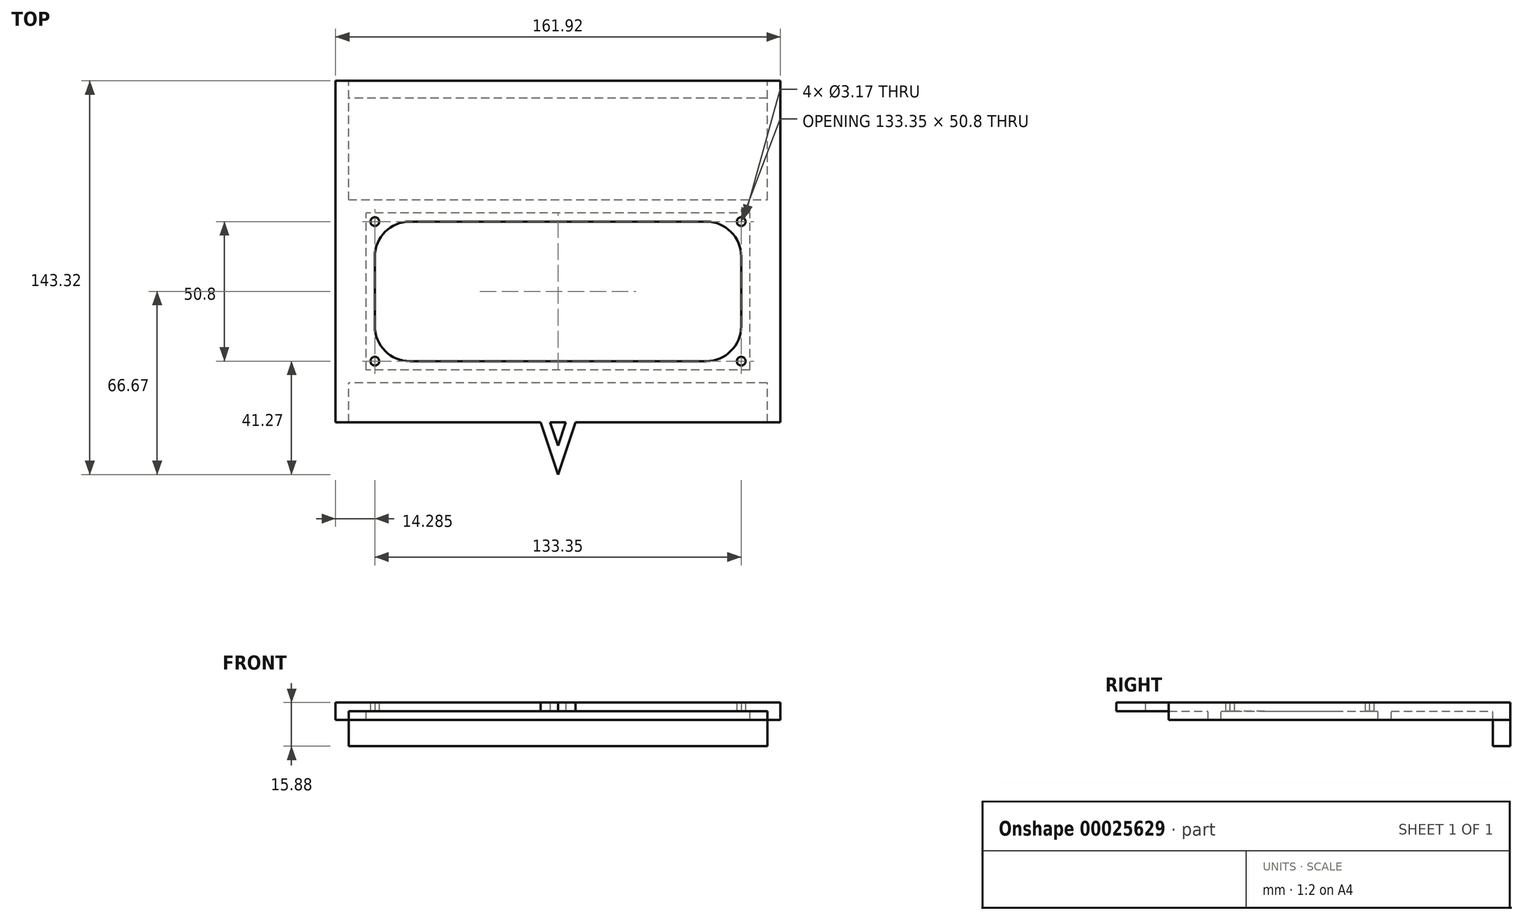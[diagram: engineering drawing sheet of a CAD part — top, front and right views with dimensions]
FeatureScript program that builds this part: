
annotation { "Feature Type Name" : "Feature", "Feature Type Description" : "" }
export const myFeature = defineFeature(function(context is Context, id is Id, definition is map)
    precondition{}
    {
        {
            var Q0;
            Q0=qCreatedBy(makeId("Top.planeOp"),FACE);
            var sketch = newSketch(context, id + "F0", { "sketchPlane" : qUnion([Q0])});
            skLineSegment(sketch, "E0.rect.bottom", {"start": v(76.2, -47.63) * mm, "end": v(6.35, -47.63) * mm});
            skLineSegment(sketch, "E0.rect.left", {"start": v(76.2, -47.62) * mm, "end": v(76.2, 47.62) * mm});
            skLineSegment(sketch, "E0.rect.right", {"start": v(-76.2, -47.63) * mm, "end": v(-76.2, 47.62) * mm});
            skPoint(sketch, "E0.rect.middle", {"position": v(0, 0) * mm});
            skCircle(sketch, "E1", {"center": v(-50.8, 9.52) * mm, "radius": 9.53 * mm});
            skCircle(sketch, "E2", {"center": v(-17.02, -9.52) * mm, "radius": 9.53 * mm});
            skCircle(sketch, "E3", {"center": v(16.76, 9.53) * mm, "radius": 9.53 * mm});
            skCircle(sketch, "E4", {"center": v(50.55, -9.52) * mm, "radius": 9.53 * mm});
            skLineSegment(sketch, "E5.rect.bottom", {"start": v(53.98, -25.4) * mm, "end": v(-53.98, -25.4) * mm});
            skLineSegment(sketch, "E5.rect.top", {"start": v(53.98, 25.4) * mm, "end": v(-53.98, 25.4) * mm});
            skLineSegment(sketch, "E5.rect.left", {"start": v(66.68, -12.7) * mm, "end": v(66.68, 12.7) * mm});
            skLineSegment(sketch, "E5.rect.right", {"start": v(-66.68, -12.7) * mm, "end": v(-66.68, 12.7) * mm});
            skPoint(sketch, "E6.visualSharp", {"position": v(-66.68, 25.4) * mm});
            skArc(sketch, "E6.filletArc", {"start": v(-53.98, 25.4) * mm, "mid": v(-62.96, 21.68) * mm, "end": v(-66.68, 12.7) * mm});
            skPoint(sketch, "E7.visualSharp", {"position": v(66.68, -25.4) * mm});
            skArc(sketch, "E7.filletArc", {"start": v(53.98, -25.4) * mm, "mid": v(62.96, -21.68) * mm, "end": v(66.68, -12.7) * mm});
            skPoint(sketch, "E8.visualSharp", {"position": v(-66.68, -25.4) * mm});
            skArc(sketch, "E8.filletArc", {"start": v(-66.68, -12.7) * mm, "mid": v(-62.96, -21.68) * mm, "end": v(-53.98, -25.4) * mm});
            skPoint(sketch, "E9.visualSharp", {"position": v(66.68, 25.4) * mm});
            skArc(sketch, "E9.filletArc", {"start": v(66.68, 12.7) * mm, "mid": v(62.96, 21.68) * mm, "end": v(53.98, 25.4) * mm});
            skLineSegment(sketch, "E10", {"start": v(-76.2, 47.62) * mm, "end": v(-76.2, 60.77) * mm});
            skLineSegment(sketch, "E11", {"start": v(76.2, 60.77) * mm, "end": v(76.2, 47.63) * mm});
            skPoint(sketch, "E12", {"position": v(-76.2, 54.42) * mm});
            skPoint(sketch, "E13", {"position": v(-76.2, 35.37) * mm});
            skLineSegment(sketch, "E14", {"start": v(-76.2, 60.77) * mm, "end": v(-76.2, 66.68) * mm});
            skLineSegment(sketch, "E15", {"start": v(76.2, 66.68) * mm, "end": v(76.2, 60.77) * mm});
            skLineSegment(sketch, "E16.rect.bottom", {"start": v(69.85, -28.57) * mm, "end": v(-69.85, -28.58) * mm});
            skLineSegment(sketch, "E16.rect.top", {"start": v(69.85, 28.58) * mm, "end": v(-69.85, 28.57) * mm});
            skLineSegment(sketch, "E16.rect.left", {"start": v(69.85, -28.58) * mm, "end": v(69.85, 28.58) * mm});
            skLineSegment(sketch, "E16.rect.right", {"start": v(-69.85, -28.58) * mm, "end": v(-69.85, 28.58) * mm});
            skLineSegment(sketch, "E17.rect.bottom", {"start": v(73.03, -33.34) * mm, "end": v(-73.03, -33.34) * mm});
            skLineSegment(sketch, "E17.rect.top", {"start": v(73.03, 33.34) * mm, "end": v(-73.03, 33.34) * mm});
            skLineSegment(sketch, "E18", {"start": v(79.38, -47.62) * mm, "end": v(76.2, -47.62) * mm});
            skLineSegment(sketch, "E19", {"start": v(-76.2, -47.63) * mm, "end": v(-79.38, -47.63) * mm});
            skCircle(sketch, "E20", {"center": v(66.68, 25.4) * mm, "radius": 1.59 * mm});
            skCircle(sketch, "E21", {"center": v(-66.68, 25.4) * mm, "radius": 1.59 * mm});
            skCircle(sketch, "E22", {"center": v(-66.68, -25.4) * mm, "radius": 1.59 * mm});
            skCircle(sketch, "E23", {"center": v(66.68, -25.4) * mm, "radius": 1.59 * mm});
            skPoint(sketch, "E24", {"position": v(0, -66.67) * mm});
            skPoint(sketch, "E25", {"position": v(0, -47.63) * mm});
            skLineSegment(sketch, "E26", {"start": v(0, -66.67) * mm, "end": v(-6.35, -47.62) * mm});
            skLineSegment(sketch, "E27", {"start": v(0, -66.67) * mm, "end": v(6.35, -47.62) * mm});
            skLineSegment(sketch, "E28", {"start": v(-2.85, -47.63) * mm, "end": v(0, -56.16) * mm});
            skLineSegment(sketch, "E29", {"start": v(0, -56.16) * mm, "end": v(2.85, -47.63) * mm});
            skLineSegment(sketch, "E30.trimOffspring", {"start": v(2.85, -47.63) * mm, "end": v(-2.85, -47.63) * mm});
            skLineSegment(sketch, "E31.trimOffspring", {"start": v(-6.35, -47.63) * mm, "end": v(-76.2, -47.63) * mm});
            skLineSegment(sketch, "E32", {"start": v(73.03, -33.34) * mm, "end": v(76.2, -33.34) * mm});
            skLineSegment(sketch, "E33", {"start": v(-73.03, -33.34) * mm, "end": v(-76.2, -33.34) * mm});
            skLineSegment(sketch, "E34", {"start": v(-73.03, 33.34) * mm, "end": v(-76.2, 33.34) * mm});
            skLineSegment(sketch, "E35", {"start": v(73.03, 33.34) * mm, "end": v(76.2, 33.34) * mm});
            skLineSegment(sketch, "E36", {"start": v(80.96, 66.68) * mm, "end": v(80.96, -47.62) * mm});
            skLineSegment(sketch, "E37", {"start": v(80.96, -47.62) * mm, "end": v(79.38, -47.62) * mm});
            skLineSegment(sketch, "E38", {"start": v(-79.38, -47.63) * mm, "end": v(-80.96, -47.63) * mm});
            skLineSegment(sketch, "E39", {"start": v(-80.96, -47.63) * mm, "end": v(-80.96, 66.68) * mm});
            skLineSegment(sketch, "E40", {"start": v(76.2, 66.68) * mm, "end": v(76.2, 70.3) * mm});
            skLineSegment(sketch, "E41", {"start": v(76.2, 70.3) * mm, "end": v(-76.2, 70.3) * mm});
            skLineSegment(sketch, "E42", {"start": v(-76.2, 70.3) * mm, "end": v(-76.2, 66.68) * mm});
            skLineSegment(sketch, "E43", {"start": v(80.96, 66.68) * mm, "end": v(80.96, 76.65) * mm});
            skLineSegment(sketch, "E44", {"start": v(80.96, 76.65) * mm, "end": v(-80.96, 76.65) * mm});
            skLineSegment(sketch, "E45", {"start": v(-80.96, 76.65) * mm, "end": v(-80.96, 66.68) * mm});
            skLineSegment(sketch, "E46", {"start": v(76.2, 70.3) * mm, "end": v(76.2, 76.65) * mm});
            skLineSegment(sketch, "E47", {"start": v(-76.2, 70.3) * mm, "end": v(-76.2, 76.65) * mm});
            skPoint(sketch, "E48.end.orphan", {"position": v(-79.38, 66.68) * mm});
            skSolve(sketch);
        }
        {
            var Q0;
            Q0=makeQuery(id+"F0.imprint","IMPRINT",FACE,{"disambiguationData":[TD([[makeQuery(id+"F0.imprint","IMPRINT",EDGE,{"derivedFrom":sQuery(id+"F0.wireOp",EDGE,"4106f267-313f-4ab9-8450-07ba015a2dba")}),1.0]])]});
            var Q1;
            Q1=makeQuery(id+"F0.imprint","IMPRINT",FACE,{"disambiguationData":[TD([[makeQuery(id+"F0.imprint","IMPRINT",EDGE,{"derivedFrom":sQuery(id+"F0.wireOp",EDGE,"E0.rect.bottom")}),-1.0]])]});
            var Q2;
            Q2=makeQuery(id+"F0.imprint","IMPRINT",FACE,{"disambiguationData":[TD([[makeQuery(id+"F0.imprint","IMPRINT",EDGE,{"derivedFrom":sQuery(id+"F0.wireOp",EDGE,"E16.rect.bottom")}),1.0]])]});
            var Q3;
            Q3=makeQuery(id+"F0.imprint","IMPRINT",FACE,{"disambiguationData":[TD([[makeQuery(id+"F0.imprint","IMPRINT",EDGE,{"derivedFrom":sQuery(id+"F0.wireOp",EDGE,"E5.rect.bottom")}),1.0]])]});
            var Q4;
            Q4=makeQuery(id+"F0.imprint","IMPRINT",FACE,{"disambiguationData":[TD([[makeQuery(id+"F0.imprint","IMPRINT",EDGE,{"derivedFrom":sQuery(id+"F0.wireOp",EDGE,"E0.rect.left")}),-1.0]])]});
            var Q5;
            Q5=makeQuery(id+"F0.imprint","IMPRINT",FACE,{"disambiguationData":[TD([[makeQuery(id+"F0.imprint","IMPRINT",EDGE,{"derivedFrom":sQuery(id+"F0.wireOp",EDGE,"E0.rect.right")}),1.0]])]});
            var Q6;
            {var subQ4=sQuery(id+"F0.wireOp",EDGE,"E10");Q6=makeQuery(id+"F0.imprint","IMPRINT",FACE,{"disambiguationData":[TD([[makeQuery(id+"F0.imprint","IMPRINT",EDGE,{"derivedFrom":subQ4}),-1.0]])]});}
            var Q7;
            Q7=makeQuery(id+"F0.imprint","IMPRINT",FACE,{"disambiguationData":[TD([[makeQuery(id+"F0.imprint","IMPRINT",EDGE,{"derivedFrom":sQuery(id+"F0.wireOp",EDGE,"E41")}),-1.0]])]});
            extrude(context, id + "F1", {"entities" : qUnion([Q0, Q1, Q2, Q3, Q4, Q5, Q6, Q7]), "depth" : 3.17 * mm});
        }
        {
            var Q0;
            Q0=makeQuery(id+"F0.imprint","IMPRINT",FACE,{"disambiguationData":[TD([[makeQuery(id+"F0.imprint","IMPRINT",EDGE,{"derivedFrom":sQuery(id+"F0.wireOp",EDGE,"E16.rect.bottom")}),1.0]])]});
            var Q1;
            Q1=makeQuery(id+"F0.imprint","IMPRINT",FACE,{"disambiguationData":[TD([[makeQuery(id+"F0.imprint","IMPRINT",EDGE,{"derivedFrom":sQuery(id+"F0.wireOp",EDGE,"E0.rect.left")}),-1.0]])]});
            var Q2;
            Q2=makeQuery(id+"F0.imprint","IMPRINT",FACE,{"disambiguationData":[TD([[makeQuery(id+"F0.imprint","IMPRINT",EDGE,{"derivedFrom":sQuery(id+"F0.wireOp",EDGE,"E0.rect.right")}),1.0]])]});
            extrude(context, id + "F2", {"entities" : qUnion([Q0, Q1, Q2]), "operationType" : NewBodyOperationType.ADD, "oppositeDirection" : true, "depth" : 3.17 * mm});
        }
        {
            var Q0;
            Q0=makeQuery(id+"F0.imprint","IMPRINT",FACE,{"disambiguationData":[TD([[makeQuery(id+"F0.imprint","IMPRINT",EDGE,{"derivedFrom":sQuery(id+"F0.wireOp",EDGE,"E41")}),-1.0]])]});
            extrude(context, id + "F3", {"entities" : qUnion([Q0]), "operationType" : NewBodyOperationType.ADD, "oppositeDirection" : true, "depth" : 12.7 * mm});
        }
    });
